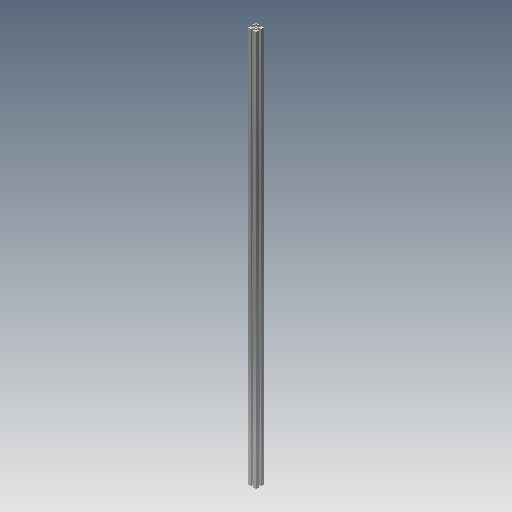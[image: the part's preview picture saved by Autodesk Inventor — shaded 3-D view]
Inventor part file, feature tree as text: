
AUTODESK INVENTOR PART (.ipt)
format: ipt  version: 2018 (Build 220112000, 112)  size: 153,600 bytes
history: native  units: mm
features: other x1, extrude x1, sketch x1
ambient origin geometry x8: Origin, YZ Plane, XZ Plane, XY Plane, X Axis, Y Axis, Z Axis, Center Point
bodies: Solid1 (feature_tree)
feature tree (3):
  other  "<userpath>\OneDrive\projects\sPhenixTileTestStand\sPhenixTileTestStand.xlsx"
  extrude  "Extrusion1"  [1 undecoded]
  sketch  "Sketch1"  dims[d0=1000.0mm d1=0.0mm]
note: 1 required parameter value undecoded (feature->parameter linkage not recoverable at this tier; creation-order binding heuristic only, values carry confidence <= 0.55)
